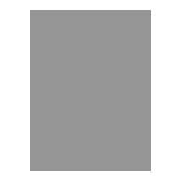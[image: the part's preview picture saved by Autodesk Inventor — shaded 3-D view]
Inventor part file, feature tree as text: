
AUTODESK INVENTOR PART (.ipt)
format: ipt  version: 2019.4 (Build 234330000, 330)  size: 115,200 bytes
history: native  units: mm (DEFAULTED — no unit token found)
features: other x4, plane x4, split x3, sketch x2
ambient origin geometry x8: Origin, YZ Plane, XZ Plane, XY Plane, X Axis, Y Axis, Z Axis, Center Point
bodies: Solid1 (feature_tree), Body (feature_tree)
feature tree (13):
  parser-record x1  (decoder bookkeeping rows leaked as tree rows — omitted from the tree; the rows remain in map.json)
  other  "Driven Length"
  other  "Start plane"
  other  "End plane"
  plane  "Work Plane6"
  split  "Split3"
  plane  "Work Plane7"
  split  "Split4"
  plane  "Work Plane8"
  split  "Split5"
  sketch  "Sketch3"  dims[d0=12.7mm]
  plane  "Work Plane3"
  sketch  "Sketch4"  dims[d1=12.7mm d2=602.702861mm d3=0.0mm d4=6.35mm d5=6.35mm d6=-6.35mm d7=596.352861mm d8=90.0deg d9=602.702861mm]
